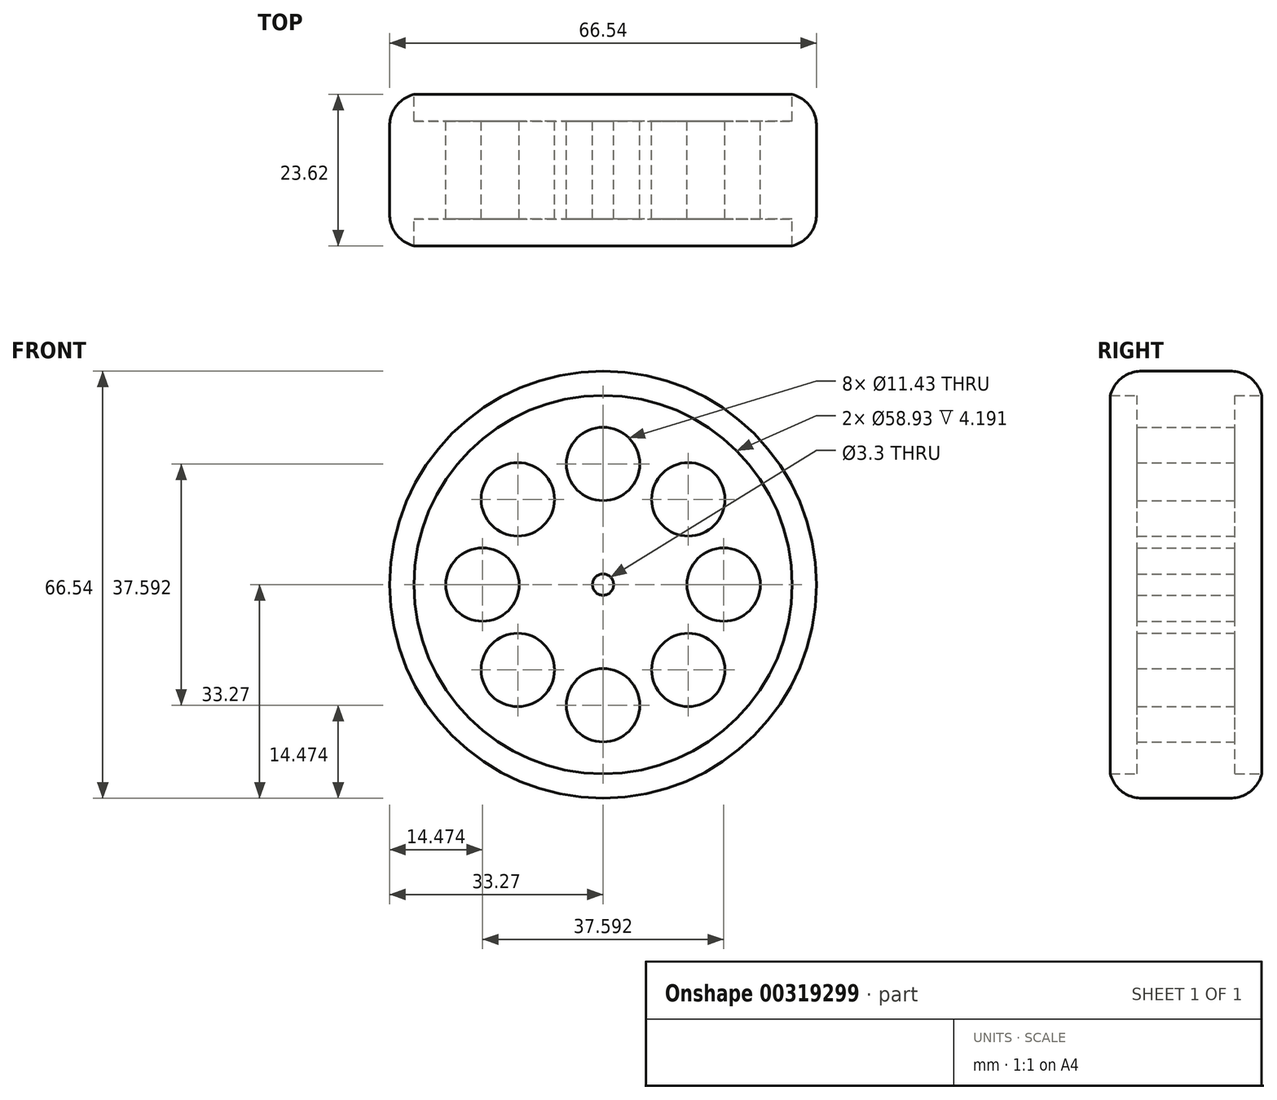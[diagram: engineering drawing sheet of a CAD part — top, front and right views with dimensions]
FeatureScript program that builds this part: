
annotation { "Feature Type Name" : "Feature", "Feature Type Description" : "" }
export const myFeature = defineFeature(function(context is Context, id is Id, definition is map)
    precondition{}
    {
        {
            var Q0;
            Q0=qCreatedBy(makeId("Front.planeOp"),FACE);
            var sketch = newSketch(context, id + "F0", { "sketchPlane" : qUnion([Q0])});
            skCircle(sketch, "E0", {"center": v(0, 0) * mm, "radius": 33.27 * mm});
            skCircle(sketch, "E1.cCircle", {"center": v(0, 0) * mm, "radius": 22.6 * mm, "construction": true});
            skLineSegment(sketch, "E1.0", {"start": v(0, -22.6) * mm, "end": v(-15.98, -15.98) * mm, "construction": true});
            skLineSegment(sketch, "E1.1", {"start": v(-15.98, -15.98) * mm, "end": v(-22.6, 0) * mm, "construction": true});
            skLineSegment(sketch, "E1.2", {"start": v(-22.6, 0) * mm, "end": v(-15.98, 15.98) * mm, "construction": true});
            skLineSegment(sketch, "E1.3", {"start": v(-15.98, 15.98) * mm, "end": v(0, 22.6) * mm, "construction": true});
            skLineSegment(sketch, "E1.4", {"start": v(0, 22.6) * mm, "end": v(15.98, 15.98) * mm, "construction": true});
            skLineSegment(sketch, "E1.5", {"start": v(15.98, 15.98) * mm, "end": v(22.6, 0) * mm, "construction": true});
            skLineSegment(sketch, "E1.6", {"start": v(22.6, 0) * mm, "end": v(15.98, -15.98) * mm, "construction": true});
            skLineSegment(sketch, "E1.7", {"start": v(15.98, -15.98) * mm, "end": v(0, -22.6) * mm, "construction": true});
            skCircle(sketch, "E2", {"center": v(0, 0) * mm, "radius": 29.46 * mm});
            skCircle(sketch, "E3.cCircle", {"center": v(0, 0) * mm, "radius": 18.8 * mm, "construction": true});
            skLineSegment(sketch, "E3.0", {"start": v(0, -18.8) * mm, "end": v(-13.3, -13.3) * mm, "construction": true});
            skLineSegment(sketch, "E3.1", {"start": v(-13.3, -13.3) * mm, "end": v(-18.8, 0) * mm, "construction": true});
            skLineSegment(sketch, "E3.2", {"start": v(-18.8, 0) * mm, "end": v(-13.3, 13.3) * mm, "construction": true});
            skLineSegment(sketch, "E3.3", {"start": v(-13.3, 13.3) * mm, "end": v(0, 18.8) * mm, "construction": true});
            skLineSegment(sketch, "E3.4", {"start": v(0, 18.8) * mm, "end": v(13.3, 13.3) * mm, "construction": true});
            skLineSegment(sketch, "E3.5", {"start": v(13.3, 13.3) * mm, "end": v(18.8, 0) * mm, "construction": true});
            skLineSegment(sketch, "E3.6", {"start": v(18.8, 0) * mm, "end": v(13.3, -13.3) * mm, "construction": true});
            skLineSegment(sketch, "E3.7", {"start": v(13.3, -13.3) * mm, "end": v(0, -18.8) * mm, "construction": true});
            skCircle(sketch, "E4", {"center": v(0, 18.8) * mm, "radius": 5.72 * mm});
            skCircle(sketch, "E5", {"center": v(-13.3, 13.3) * mm, "radius": 5.72 * mm});
            skCircle(sketch, "E6", {"center": v(13.3, 13.3) * mm, "radius": 5.72 * mm});
            skCircle(sketch, "E7", {"center": v(18.8, 0) * mm, "radius": 5.72 * mm});
            skCircle(sketch, "E8", {"center": v(13.3, -13.3) * mm, "radius": 5.72 * mm});
            skCircle(sketch, "E9", {"center": v(0, -18.8) * mm, "radius": 5.72 * mm});
            skCircle(sketch, "E10", {"center": v(-13.3, -13.3) * mm, "radius": 5.72 * mm});
            skCircle(sketch, "E11", {"center": v(-18.8, 0) * mm, "radius": 5.72 * mm});
            skCircle(sketch, "E12", {"center": v(0, 0) * mm, "radius": 1.65 * mm});
            skSolve(sketch);
        }
        {
            var Q0;
            Q0=makeQuery(id+"F0.imprint","IMPRINT",FACE,{"disambiguationData":[TD([[makeQuery(id+"F0.imprint","IMPRINT",EDGE,{"derivedFrom":sQuery(id+"F0.wireOp",EDGE,"E2")}),1.0]])]});
            extrude(context, id + "F1", {"entities" : qUnion([Q0]), "endBound" : BoundingType.SYMMETRIC, "depth" : 15.24 * mm});
        }
        {
            var Q0;
            Q0 = qSketchRegion(id + "F0", true);
            extrude(context, id + "F2", {"entities" : qUnion([Q0]), "operationType" : NewBodyOperationType.ADD, "endBound" : BoundingType.SYMMETRIC, "depth" : 23.62 * mm});
        }
        {
            var Q0;
            Q0=makeQuery(id+"F2.opExtrude","SWEPT_FACE",FACE,{"disambiguationData":[OSD([sQuery(id+"F0.wireOp",EDGE,"E0")])]});
            fillet(context, id + "F3", {"entities" : qUnion([Q0]), "radius" : 5.08 * mm, "tangentPropagation" : true, "allowEdgeOverflow" : false});
        }
    });
